# Revit family: Sanitary_Showers_hansgrohe_27804007-Vernis-Blend-Ceiling-connector_
name_source: partatom
category: Plumbing Fixtures
revit_build: Autodesk Revit 2015 (Build: 20140322_1515(x64)
units: mm (PartAtom-declared; Revit-internal decimal feet)

## types (1)
- Chrome 000
    BIMobject category = Showers
    BIMobject category code = sanitary-showers
    BIMobject main category = Sanitary
    BIMobject main category code = sanitary
    Brand url = http://www.hansgrohe-int.com
    Design country = Germany
    Edition number = 1
    GTIN code = https://4059625282090
    IFC Classification = Sanitary Terminal
    Manufacturer country = Germany
    Manufacturer name = hansgrohe
    Material main = Chrome
    Product Guid = cd81bea0-0aed-4aab-a084-4cb6d55150ab
    Product SKU = 27804007
    Product certification = https://www.hansgrohe.com.cn
    Product data url = https://bimobject.com
    Product family = Shower arms
    Product group = Vernis Blend
    Product name = 27804007 Vernis Blend Ceiling connector 10 cm
    Product url = https://www.hansgrohe.com.cn
    QR code = http://bimobject.com
    Technical description = https://www.hansgrohe.com.cn

## geometry (parser evidence)
native form markers: Blend x5, Sweep x3
no freeform markers — native parametric forms only
